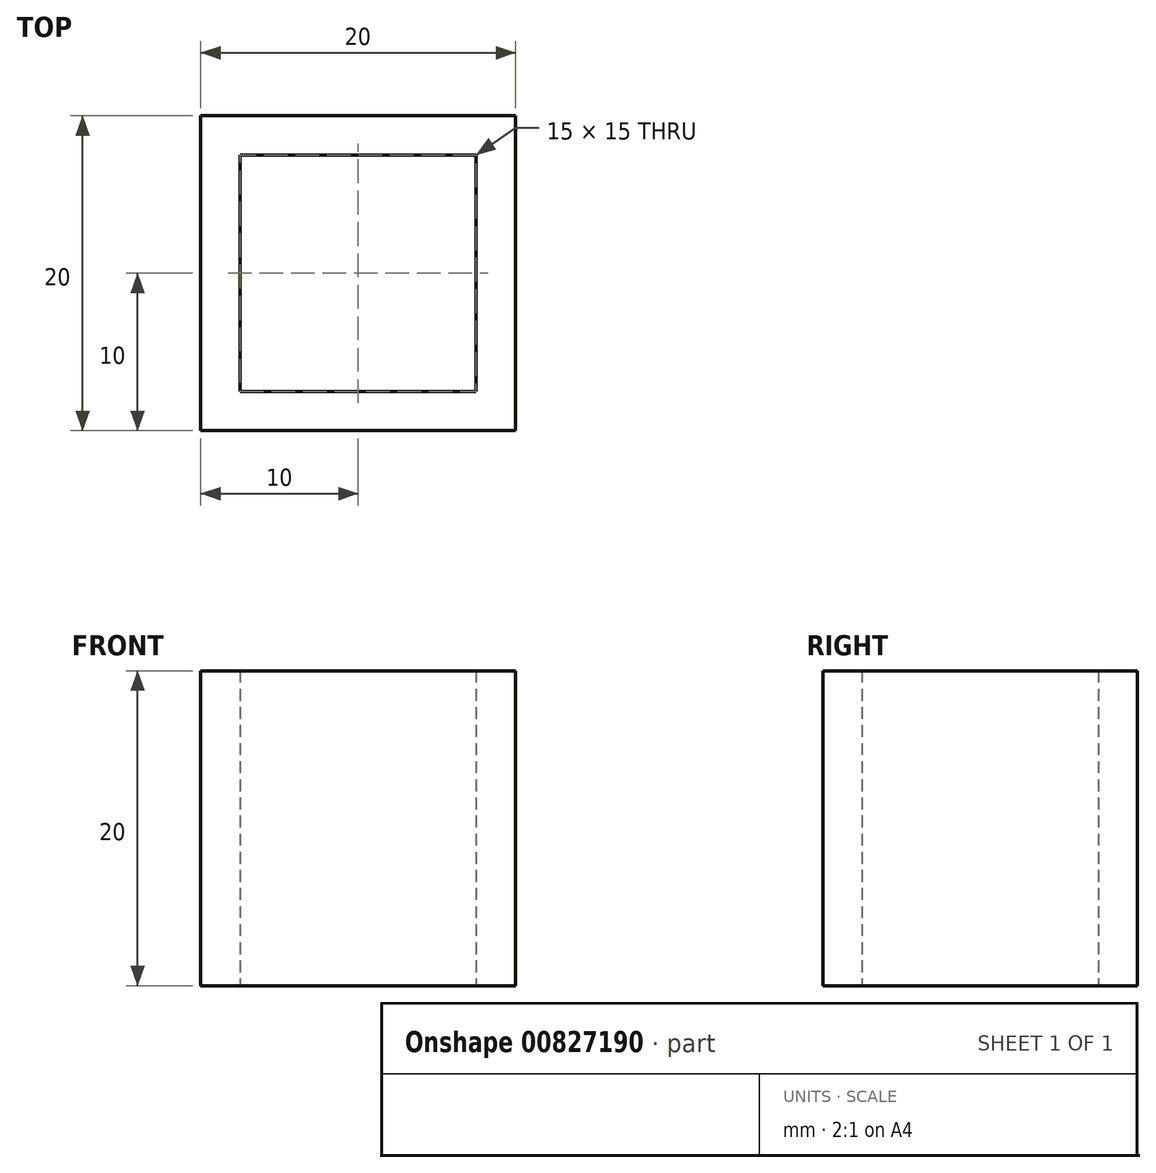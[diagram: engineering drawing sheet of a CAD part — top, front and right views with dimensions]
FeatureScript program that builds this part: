
annotation { "Feature Type Name" : "Feature", "Feature Type Description" : "" }
export const myFeature = defineFeature(function(context is Context, id is Id, definition is map)
    precondition{}
    {
        {
            var Q0;
            Q0=qCreatedBy(makeId("Top.planeOp"),FACE);
            var sketch = newSketch(context, id + "F0", { "sketchPlane" : qUnion([Q0])});
            skLineSegment(sketch, "E0.bottom", {"start": v(10, -10) * mm, "end": v(-10, -10) * mm});
            skLineSegment(sketch, "E0.top", {"start": v(10, 10) * mm, "end": v(-10, 10) * mm});
            skLineSegment(sketch, "E0.left", {"start": v(10, -10) * mm, "end": v(10, 10) * mm});
            skLineSegment(sketch, "E0.right", {"start": v(-10, -10) * mm, "end": v(-10, 10) * mm});
            skPoint(sketch, "E0.middle", {"position": v(0, 0) * mm});
            skSolve(sketch);
        }
        {
            var Q0;
            Q0=makeQuery(id+"F0.imprint","IMPRINT",FACE,{"disambiguationData":[TD([[makeQuery(id+"F0.imprint","IMPRINT",EDGE,{"derivedFrom":sQuery(id+"F0.wireOp",EDGE,"E0.bottom")}),-1.0]])]});
            extrude(context, id + "F1", {"entities" : qUnion([Q0]), "depth" : 20 * mm, "offsetDistance" : 25 * mm});
        }
        {
            var Q0;
            Q0=makeQuery(id+"F1.opExtrude","CAP_FACE",FACE,{"disambiguationData":[OSD([sQuery(id+"F0.wireOp",EDGE,"E0.bottom"),sQuery(id+"F0.wireOp",EDGE,"E0.top"),sQuery(id+"F0.wireOp",EDGE,"E0.left"),sQuery(id+"F0.wireOp",EDGE,"E0.right")])],"isStart":false});
            var Q1;
            Q1=makeQuery(id+"F1.opExtrude","CAP_FACE",FACE,{"disambiguationData":[OSD([sQuery(id+"F0.wireOp",EDGE,"E0.bottom"),sQuery(id+"F0.wireOp",EDGE,"E0.top"),sQuery(id+"F0.wireOp",EDGE,"E0.left"),sQuery(id+"F0.wireOp",EDGE,"E0.right")])],"isStart":true});
            var Q2;
            Q2=makeQuery(id+"F1.opExtrude","SWEPT_BODY",BODY,{"disambiguationData":[OSD([sQuery(id+"F0.wireOp",EDGE,"E0.bottom"),sQuery(id+"F0.wireOp",EDGE,"E0.top"),sQuery(id+"F0.wireOp",EDGE,"E0.left"),sQuery(id+"F0.wireOp",EDGE,"E0.right")])]});
            shell(context, id + "F2", {"entities" : qUnion([Q0, Q1]), "parts" : qUnion([Q2]), "thickness" : 2.5 * mm});
        }
    });
